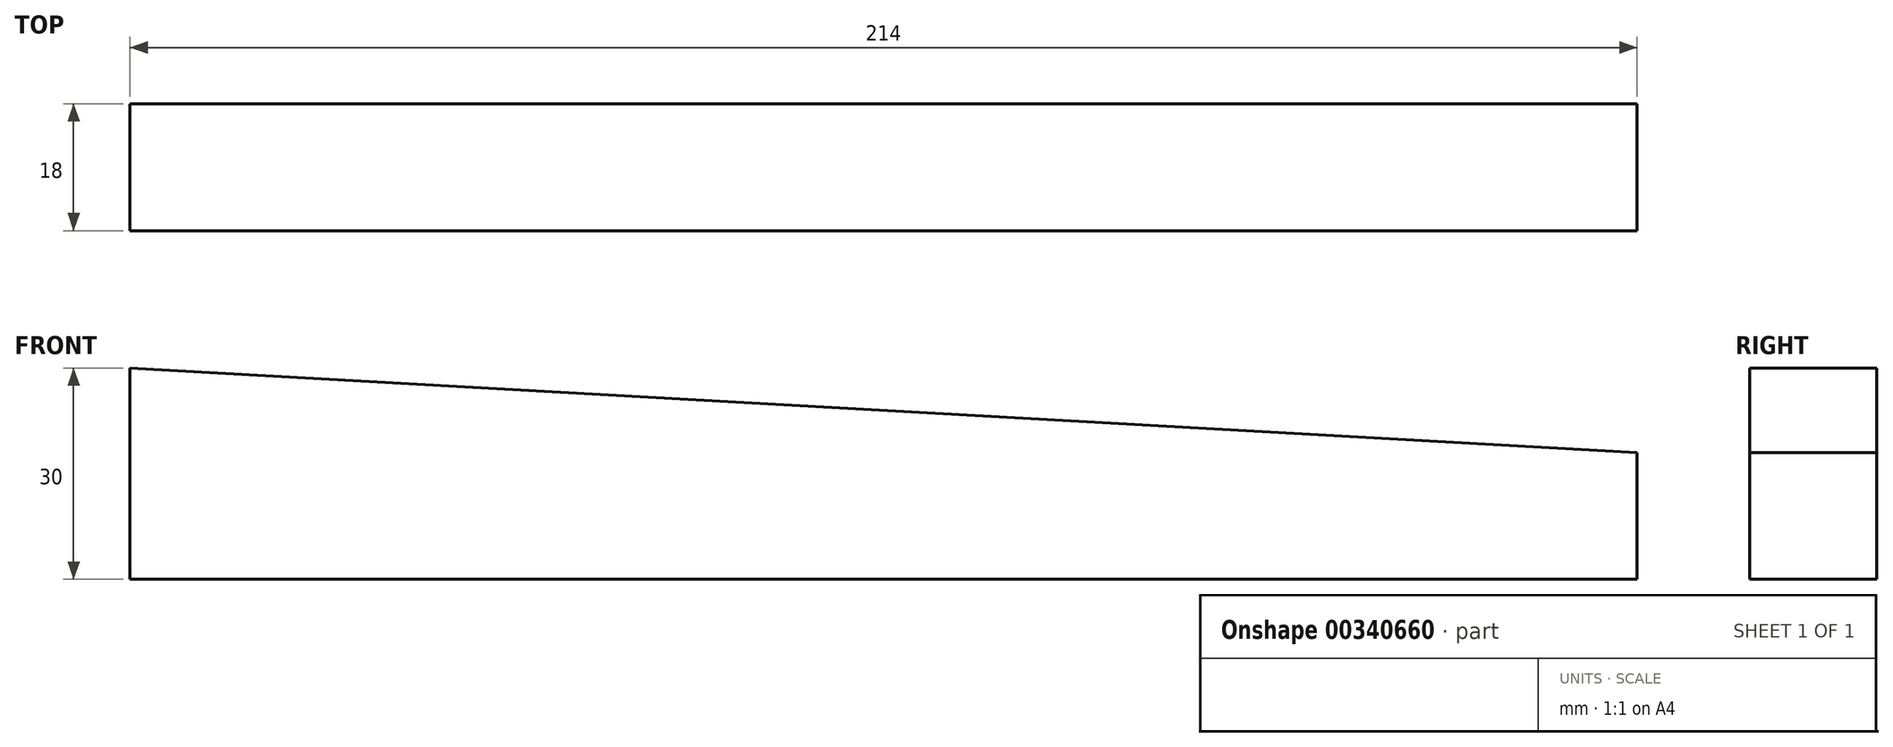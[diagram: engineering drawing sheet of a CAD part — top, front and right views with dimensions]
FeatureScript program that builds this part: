
annotation { "Feature Type Name" : "Feature", "Feature Type Description" : "" }
export const myFeature = defineFeature(function(context is Context, id is Id, definition is map)
    precondition{}
    {
        {
            var Q0;
            Q0=qCreatedBy(makeId("Front.planeOp"),FACE);
            var sketch = newSketch(context, id + "F0", { "sketchPlane" : qUnion([Q0])});
            skLineSegment(sketch, "E0.top", {"start": v(-94.9, -37.3) * mm, "end": v(119.1, -37.3) * mm});
            skLineSegment(sketch, "E0.left", {"start": v(-94.9, -7.3) * mm, "end": v(-94.9, -37.3) * mm});
            skLineSegment(sketch, "E0.right", {"start": v(119.1, -19.3) * mm, "end": v(119.1, -37.3) * mm});
            skLineSegment(sketch, "E1", {"start": v(-94.9, -7.3) * mm, "end": v(119.1, -19.3) * mm});
            skPoint(sketch, "E2.orphan", {"position": v(119.1, -7.3) * mm});
            skSolve(sketch);
        }
        {
            var Q0;
            Q0=makeQuery(id+"F0.imprint","IMPRINT",FACE,{"disambiguationData":[TD([[makeQuery(id+"F0.imprint","IMPRINT",EDGE,{"derivedFrom":sQuery(id+"F0.wireOp",EDGE,"E0.top")}),1.0]])]});
            extrude(context, id + "F1", {"entities" : qUnion([Q0]), "depth" : 18 * mm});
        }
    });
